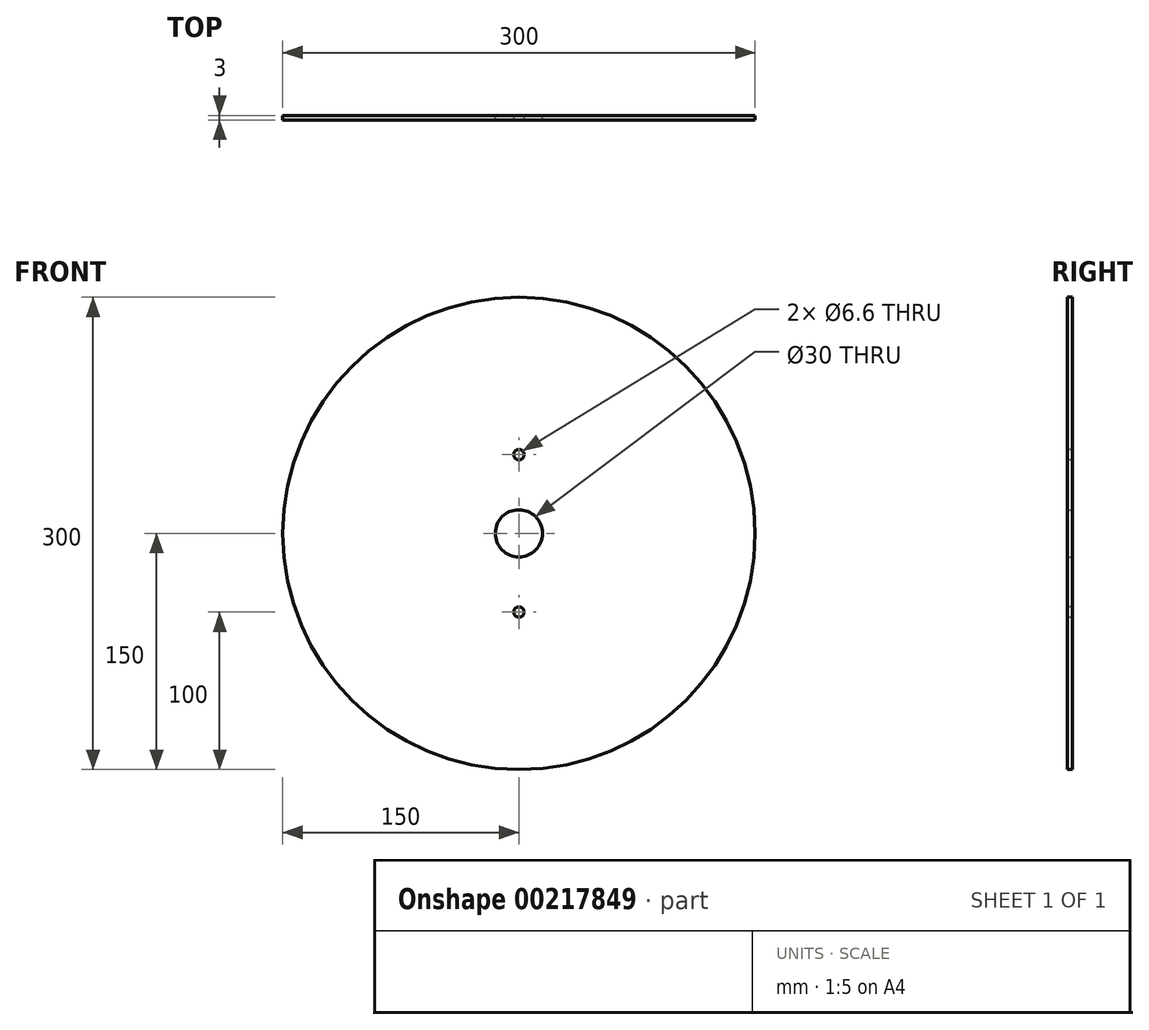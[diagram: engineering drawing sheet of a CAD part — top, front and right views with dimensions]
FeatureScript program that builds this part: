
annotation { "Feature Type Name" : "Feature", "Feature Type Description" : "" }
export const myFeature = defineFeature(function(context is Context, id is Id, definition is map)
    precondition{}
    {
        {
            var Q0;
            Q0=qCreatedBy(makeId("Front.planeOp"),FACE);
            var sketch = newSketch(context, id + "F0", { "sketchPlane" : qUnion([Q0])});
            skCircle(sketch, "E0", {"center": v(0, 0) * mm, "radius": 15 * mm});
            skCircle(sketch, "E1", {"center": v(0, 0) * mm, "radius": 150 * mm});
            skSolve(sketch);
        }
        {
            var Q0;
            Q0 = qSketchRegion(id + "F0", true);
            extrude(context, id + "F1", {"entities" : qUnion([Q0]), "depth" : 3 * mm});
        }
        {
            var Q0;
            Q0=makeQuery(id+"F1.opExtrude","CAP_FACE",FACE,{"disambiguationData":[OSD([sQuery(id+"F0.wireOp",EDGE,"E0"),sQuery(id+"F0.wireOp",EDGE,"E1")])],"isStart":false});
            var sketch = newSketch(context, id + "F2", { "sketchPlane" : qUnion([Q0])});
            skCircle(sketch, "E2", {"center": v(0, 50) * mm, "radius": 3.3 * mm});
            skCircle(sketch, "E3", {"center": v(0, -50) * mm, "radius": 3.3 * mm});
            skSolve(sketch);
        }
        {
            var Q0;
            Q0=sQuery(id+"F2.wireOp",VERTEX,"E2.center");
            var Q1;
            Q1=sQuery(id+"F2.wireOp",VERTEX,"E3.center");
            var Q2;
            Q2=makeQuery(id+"F1.opExtrude","SWEPT_BODY",BODY,{"disambiguationData":[OSD([sQuery(id+"F0.wireOp",EDGE,"E0"),sQuery(id+"F0.wireOp",EDGE,"E1")])]});
            hole(context, id + "F3", {"style" : HoleStyle.SIMPLE, "endStyle" : HoleEndStyle.BLIND, "standardTappedOrClearance" : lookupTablePath({ "standard" : "ISO", "fit" : "Normal", "size" : "M6", "type" : "Clearance" }), "standardBlindInLast" : lookupTablePath({ "fit" : "Standard", "standard" : "ISO", "size" : "M6", "type" : "Clearance" }), "holeDiameter" : 6.6 * mm, "holeDepth" : 14.5 * mm, "tappedDepth" : 11.5 * mm, "tapClearance" : 3, "startFromSketch" : true, "locations" : qUnion([Q0, Q1]), "scope" : qUnion([Q2])});
        }
    });
